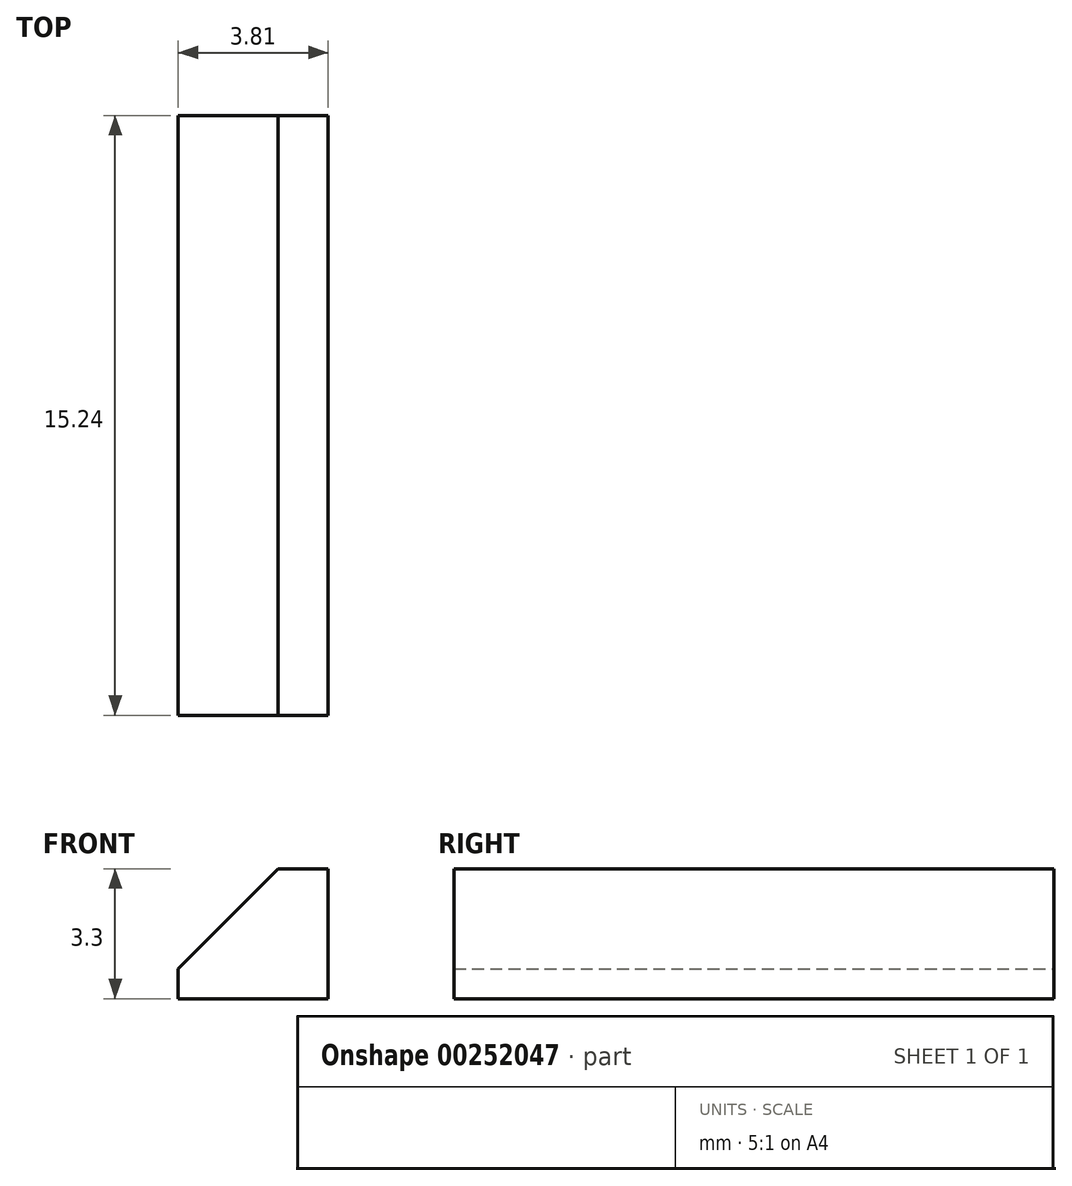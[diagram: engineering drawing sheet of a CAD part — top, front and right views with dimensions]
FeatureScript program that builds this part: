
annotation { "Feature Type Name" : "Feature", "Feature Type Description" : "" }
export const myFeature = defineFeature(function(context is Context, id is Id, definition is map)
    precondition{}
    {
        {
            var Q0;
            Q0=qCreatedBy(makeId("Right.planeOp"),FACE);
            var sketch = newSketch(context, id + "F0", { "sketchPlane" : qUnion([Q0])});
            skLineSegment(sketch, "E0.bottom", {"start": v(-7.62, 1.65) * mm, "end": v(7.62, 1.65) * mm});
            skLineSegment(sketch, "E0.top", {"start": v(-7.62, -1.65) * mm, "end": v(7.62, -1.65) * mm});
            skLineSegment(sketch, "E0.left", {"start": v(-7.62, 1.65) * mm, "end": v(-7.62, -1.65) * mm});
            skLineSegment(sketch, "E0.right", {"start": v(7.62, 1.65) * mm, "end": v(7.62, -1.65) * mm});
            skPoint(sketch, "E0.middle", {"position": v(0, 0) * mm});
            skSolve(sketch);
        }
        {
            var Q0;
            Q0 = qSketchRegion(id + "F0", true);
            extrude(context, id + "F1", {"entities" : qUnion([Q0]), "depth" : 3.8 * mm});
        }
        {
            var Q0;
            Q0=makeQuery(id+"F1.opExtrude","CAP_EDGE",EDGE,{"disambiguationData":[OSD([sQuery(id+"F0.wireOp",EDGE,"E0.bottom")])],"isStart":true});
            chamfer(context, id + "F2", {"entities" : qUnion([Q0]), "width" : 2.54 * mm, "tangentPropagation" : true});
        }
    });
